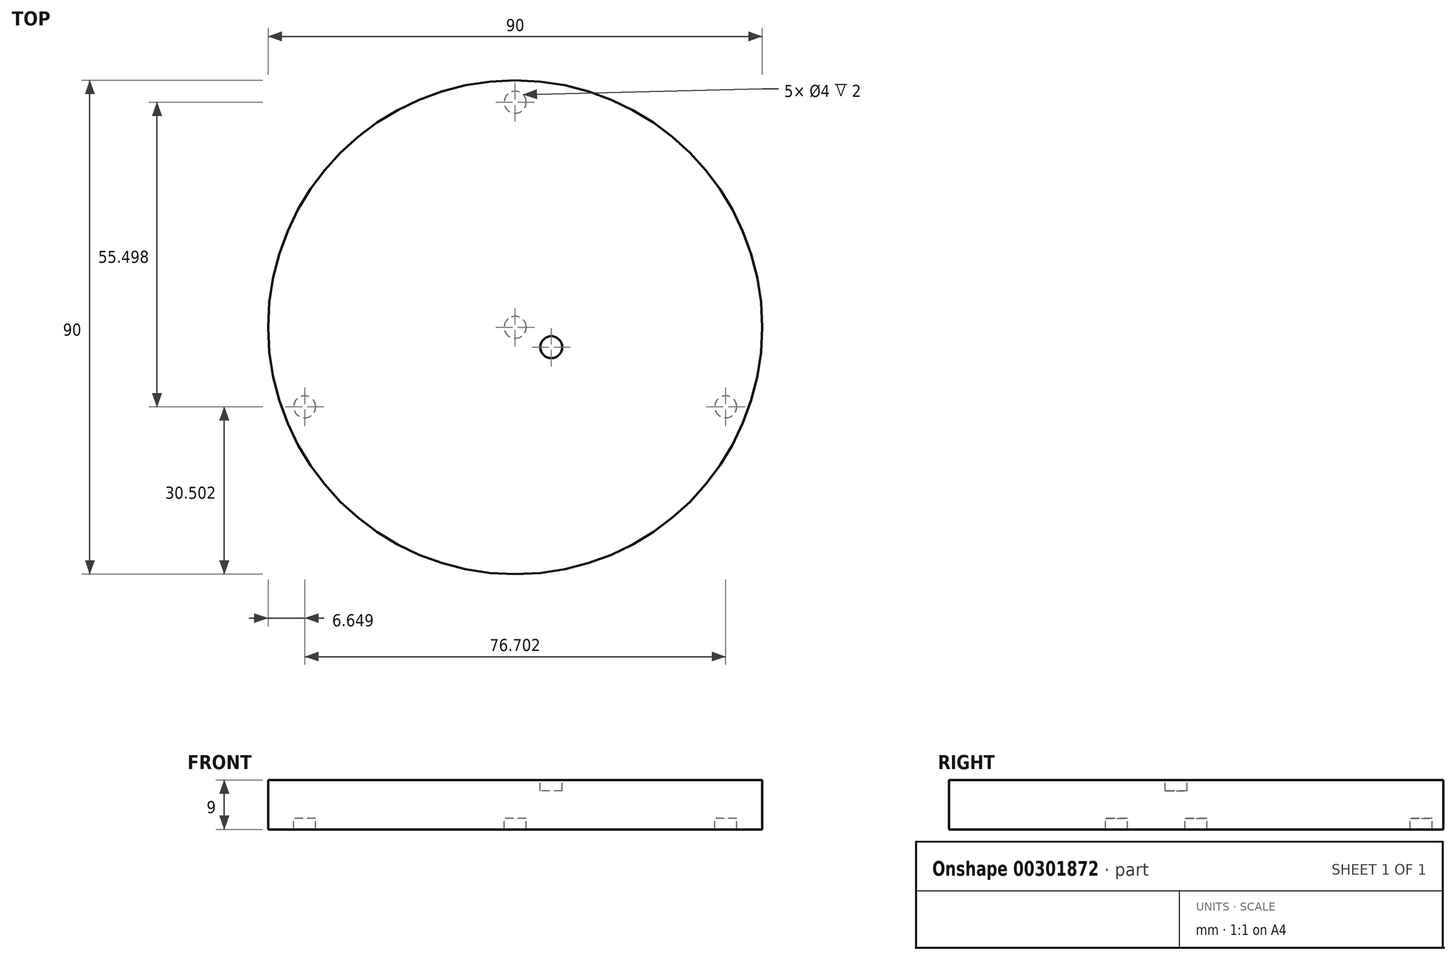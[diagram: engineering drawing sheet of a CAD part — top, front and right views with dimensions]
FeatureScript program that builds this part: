
annotation { "Feature Type Name" : "Feature", "Feature Type Description" : "" }
export const myFeature = defineFeature(function(context is Context, id is Id, definition is map)
    precondition{}
    {
        {
            var Q0;
            Q0=qCreatedBy(makeId("Top.planeOp"),FACE);
            var sketch = newSketch(context, id + "F0", { "sketchPlane" : qUnion([Q0])});
            skCircle(sketch, "E0", {"center": v(0, 0) * mm, "radius": 45 * mm});
            skCircle(sketch, "E1", {"center": v(0, 0) * mm, "radius": 41 * mm, "construction": true});
            skCircle(sketch, "E2", {"center": v(0, 0) * mm, "radius": 2 * mm});
            skCircle(sketch, "E3", {"center": v(0, 41) * mm, "radius": 2 * mm});
            skCircle(sketch, "E4", {"center": v(-38.35, -14.5) * mm, "radius": 2 * mm});
            skCircle(sketch, "E5", {"center": v(38.35, -14.5) * mm, "radius": 2 * mm});
            skCircle(sketch, "E6", {"center": v(6.56, -3.63) * mm, "radius": 2 * mm});
            skSolve(sketch);
        }
        {
            var Q0;
            Q0 = qSketchRegion(id + "F0", true);
            var Q1;
            Q1=makeQuery(id+"F0.imprint","IMPRINT",FACE,{"disambiguationData":[TD([[makeQuery(id+"F0.imprint","IMPRINT",EDGE,{"derivedFrom":sQuery(id+"F0.wireOp",EDGE,"E6")}),1.0]])]});
            extrude(context, id + "F1", {"entities" : qUnion([Q0, Q1]), "oppositeDirection" : true, "depth" : 9 * mm});
        }
        {
            var Q0;
            Q0=makeQuery(id+"F0.imprint","IMPRINT",FACE,{"disambiguationData":[TD([[makeQuery(id+"F0.imprint","IMPRINT",EDGE,{"derivedFrom":sQuery(id+"F0.wireOp",EDGE,"E2")}),1.0]])]});
            var Q1;
            Q1=makeQuery(id+"F0.imprint","IMPRINT",FACE,{"disambiguationData":[TD([[makeQuery(id+"F0.imprint","IMPRINT",EDGE,{"derivedFrom":sQuery(id+"F0.wireOp",EDGE,"E3")}),1.0]])]});
            var Q2;
            Q2=makeQuery(id+"F0.imprint","IMPRINT",FACE,{"disambiguationData":[TD([[makeQuery(id+"F0.imprint","IMPRINT",EDGE,{"derivedFrom":sQuery(id+"F0.wireOp",EDGE,"E5")}),1.0]])]});
            var Q3;
            Q3=makeQuery(id+"F0.imprint","IMPRINT",FACE,{"disambiguationData":[TD([[makeQuery(id+"F0.imprint","IMPRINT",EDGE,{"derivedFrom":sQuery(id+"F0.wireOp",EDGE,"E4")}),1.0]])]});
            extrude(context, id + "F2", {"entities" : qUnion([Q0, Q1, Q2, Q3]), "operationType" : NewBodyOperationType.ADD, "oppositeDirection" : true, "depth" : 7 * mm});
        }
        {
            var Q0;
            Q0=makeQuery(id+"F0.imprint","IMPRINT",FACE,{"disambiguationData":[TD([[makeQuery(id+"F0.imprint","IMPRINT",EDGE,{"derivedFrom":sQuery(id+"F0.wireOp",EDGE,"E6")}),1.0]])]});
            extrude(context, id + "F3", {"entities" : qUnion([Q0]), "operationType" : NewBodyOperationType.REMOVE, "oppositeDirection" : true, "depth" : 2 * mm});
        }
    });
